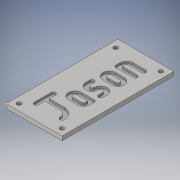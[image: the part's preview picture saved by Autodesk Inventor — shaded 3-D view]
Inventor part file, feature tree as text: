
AUTODESK INVENTOR PART (.ipt)
format: ipt  version: 2016 (Build 200138000, 138)  size: 179,712 bytes
history: native  units: in
note: dims shown in document units (in); Inventor stores cm internally (conversion verified against a paired STEP export)
features: sketch x3, extrude x2
ambient origin geometry x8: Origin, YZ Plane, XZ Plane, XY Plane, X Axis, Y Axis, Z Axis, Center Point
bodies: Solid1 (feature_tree)
feature tree (5):
  extrude  "Extrusion1"  Depth=0.125in TaperAngle=0.0deg
  sketch  "Sketch2"
  sketch  "Sketch3"
  extrude  "Extrusion2"  [1 undecoded]
  sketch  "Sketch1"  dims[d0=0.25in d1=0.0in d2=0.125in d3=0.0in]
note: 1 required parameter value undecoded (feature->parameter linkage not recoverable at this tier; creation-order binding heuristic only, values carry confidence <= 0.55)
